# Revit family: FU_Stool_Sandler_VARYA TAPIZ_3-1
name_source: partatom
category: Furniture
units: mm (PartAtom-declared; Revit-internal decimal feet)

## family parameters
Always vertical = No
Cut with Voids When Loaded = No
OmniClass Number = 23.21.23.15.17
Room Calculation Point = No
Shared = No
Work Plane-Based = Yes

## types (1)
- VARYA Tapiz 3.1
    401D = No
    401G = No
    BIMobject category = Chair
    BIMobject category code = furniture-chair
    BIMobject main category = Furniture
    BIMobject main category code = furniture
    Brand url = https://www.sandlerseating.com
    Default Elevation = 1219.2 mm  [stored 4 ft]
    Description = Four leg barstool with upholstered seat and back, and steel base. Greenguard Certified.
    Edition number = 1
    Frame = BS18
    Frame Material = Epoxy - M1_B00 - Black
    Height Frame = 770 mm  [stored 2.52625 ft]
    IFC Classification = Furnishing Element
    Manufacturer = Sandler
    Manufacturer country = USA
    Manufacturer name = Sandler
    Masterformat 2014 Code = 12 48 43.13
    Masterformat 2014 Description = Chair Mats
    Model = VARYA Tapiz 3.1
    OmniClass Code = 23-21 23 15 17
    Product Guid = ??
    Product SKU = ??
    Product data url = https://www.sandlerseating.com
    Product family = Furniture
    Product group = Chair
    Product name = VARYA Tapiz 3.1
    QR code = https://www.sandlerseating.com
    Seat Material = Fabric - Mainline Flax - Bayswater MLF24
    Shell = TP04_Tapiz
    Uniformat II Description = Movable Furnishings
    width = 480 mm

note: [stored X ft] marks values corroborated as IEEE doubles in the binary element streams (Revit-internal decimal feet)

## geometry (parser evidence)
native form markers: Sweep x8
no freeform markers — native parametric forms only
